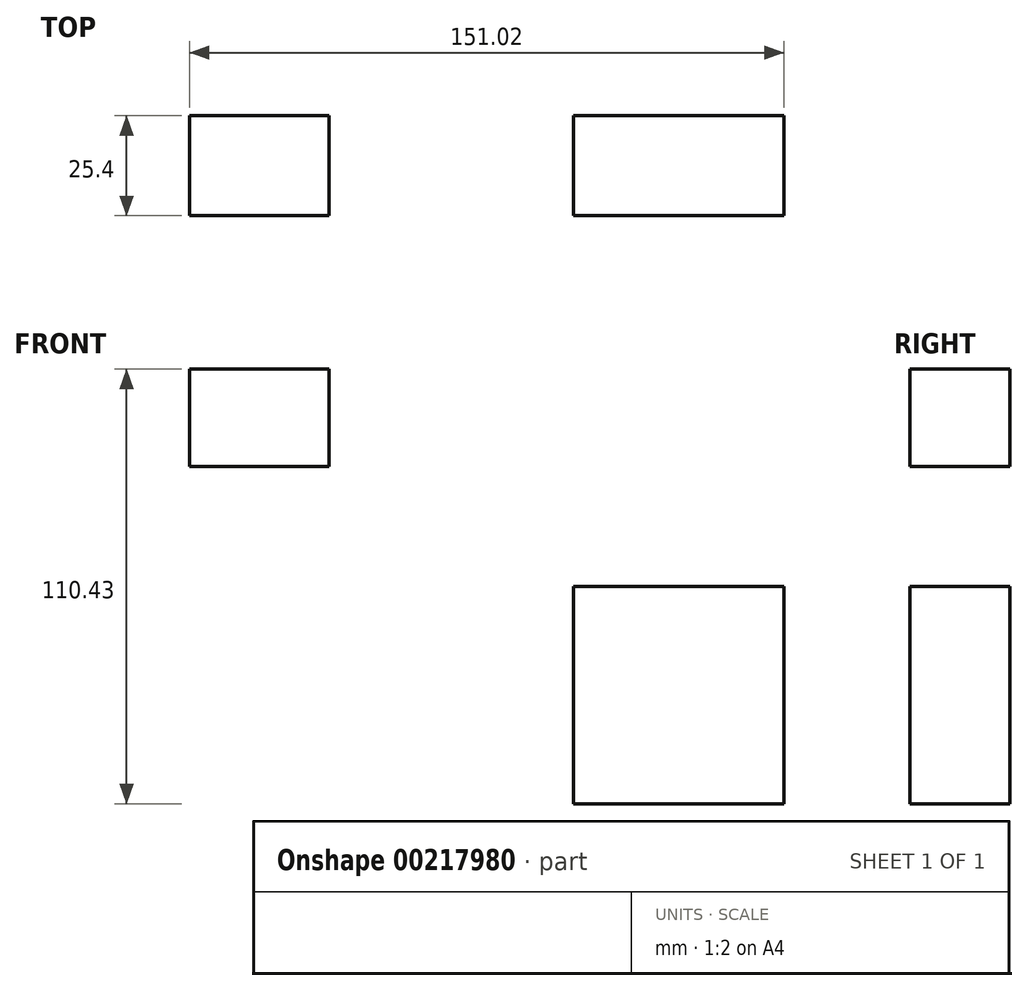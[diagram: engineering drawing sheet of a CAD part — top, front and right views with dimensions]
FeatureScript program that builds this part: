
annotation { "Feature Type Name" : "Feature", "Feature Type Description" : "" }
export const myFeature = defineFeature(function(context is Context, id is Id, definition is map)
    precondition{}
    {
        {
            var Q0;
            Q0=qCreatedBy(makeId("Front.planeOp"),FACE);
            var sketch = newSketch(context, id + "F0", { "sketchPlane" : qUnion([Q0])});
            skLineSegment(sketch, "E0.bottom", {"start": v(-67, 55.17) * mm, "end": v(-31.5, 55.17) * mm});
            skLineSegment(sketch, "E0.top", {"start": v(-67, 30.41) * mm, "end": v(-31.5, 30.41) * mm});
            skLineSegment(sketch, "E0.left", {"start": v(-67, 55.17) * mm, "end": v(-67, 30.41) * mm});
            skLineSegment(sketch, "E0.right", {"start": v(-31.5, 55.17) * mm, "end": v(-31.5, 30.41) * mm});
            skLineSegment(sketch, "E1.bottom", {"start": v(30.5, 0) * mm, "end": v(84.01, 0) * mm});
            skLineSegment(sketch, "E1.top", {"start": v(30.5, -55.26) * mm, "end": v(84.01, -55.26) * mm});
            skLineSegment(sketch, "E1.left", {"start": v(30.5, 0) * mm, "end": v(30.5, -55.26) * mm});
            skLineSegment(sketch, "E1.right", {"start": v(84.01, 0) * mm, "end": v(84.01, -55.26) * mm});
            skSolve(sketch);
        }
        {
            var Q0;
            Q0 = qSketchRegion(id + "F0", true);
            extrude(context, id + "F1", {"entities" : qUnion([Q0]), "depth" : 25.4 * mm});
        }
    });
